# Revit family: O2IM -10BF
name_source: partatom
category: Mechanical Equipment
units: mm (PartAtom-declared; Revit-internal decimal feet)

## family parameters
Always vertical = Yes
Cut with Voids When Loaded = No
OmniClass Number = 23.40.40.11.17
OmniClass Title = Refrigerated Cases
Part Type = Normal
Room Calculation Point = No
Round Connector Dimension = Use Radius
Shared = No
Work Plane-Based = Yes

## types (6) — shared parameters
BASE HEIGHT = 10"
CERTIFICATIONS = NSF 7, UL471, CSA
DATE = 05/22/12
DIEBOARD HEIGHT = 0"
DRAIN LINE CONNECTION = Drain Connection
DRAIN LINE DIAMETER = 2"
DRAIN LINE RADIUS = 1"
DRAIN PIPE LENGTH = 0"
DRAIN PIPE TYPE = PVC
DRIP PAN PLUMB TYPE = HARD
Default Elevation = 48"
Description = Wide Multi-Deck Island Merchandiser
EQUIPMENT MARK = O2IM
HEIGHT = 45 3/16"
Keynote = Deli / Meat
LIQUID LINE CONNECTION = LIQUID LINE CONNECTION
LIQUID LINE DIAMETER = 0"
LIQUID LINE RADIUS = 0"
Manufacturer = HILL PHOENIX
PRESSURE REGULATOR = 0.00 psi
REF PLANE FRONT BACK = 39 7/8"
SIZE OF COLD WATER HOOK UP = 0"
SIZE OF HOT WATER HOOK-UP = 0"
SUCTION LINE CONNECTION = SUCTION LINE CONNECTION
SUCTION LINE DIAMETER = 1"
SUCTION LINE RADIUS = 0"
TOEKICK HEIGHT = 5 1/2"
TOEKICK INSET = 1 1/2"
URL = http://www.hillphoenix.com
WIDTH = 79 3/4"

## per-type parameters (varying)
| type | LEGEND NUMBER | LENGTH | Model | REF PLANE LEFT RIGHT |
| O2IM-8, 10",12",14",16" SD | O2IM-8' | 105 5/8" | O2IM-8' | 52 13/16" |
| O2IM-12',10",12",14",16" SD | O2IM-12' | 153 1/2" | O2IM-12' | 76 3/4" |
| O2IM 8', TOP SILL SD | O2IM-8' | 105 5/8" | O2IM-8' | 52 13/16" |
| O2IM 8', 8" SD | O2IM-8' | 105 5/8" | O2IM-8' | 52 13/16" |
| O2IM 12', TOP SILL SD | O2IM-12' | 153 1/2" | O2IM-12' | 76 3/4" |
| O2IM 12', 8" SD | O2IM-12' | 153 1/2" | O2IM-12' | 76 3/4" |

## geometry (parser evidence)
native form markers: Blend x2, Sweep x7
no freeform markers — native parametric forms only
